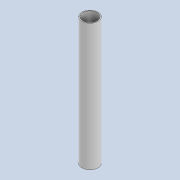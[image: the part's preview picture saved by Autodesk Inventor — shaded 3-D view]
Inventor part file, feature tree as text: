
AUTODESK INVENTOR PART (.ipt)
format: ipt  version: 2020 (Build 240168000, 168)  size: 74,240 bytes
history: native  units: mm
features: extrude x1, sketch x1
ambient origin geometry x8: Origin, YZ Plane, XZ Plane, XY Plane, X Axis, Y Axis, Z Axis, Center Point
bodies: Solid1 (feature_tree)
feature tree (2):
  extrude  "Extrusion1"  Depth=300.0mm
  sketch  "Sketch1"  dims[d0=38.0mm d1=34.0mm d2=300.0mm d3=0.0mm]
